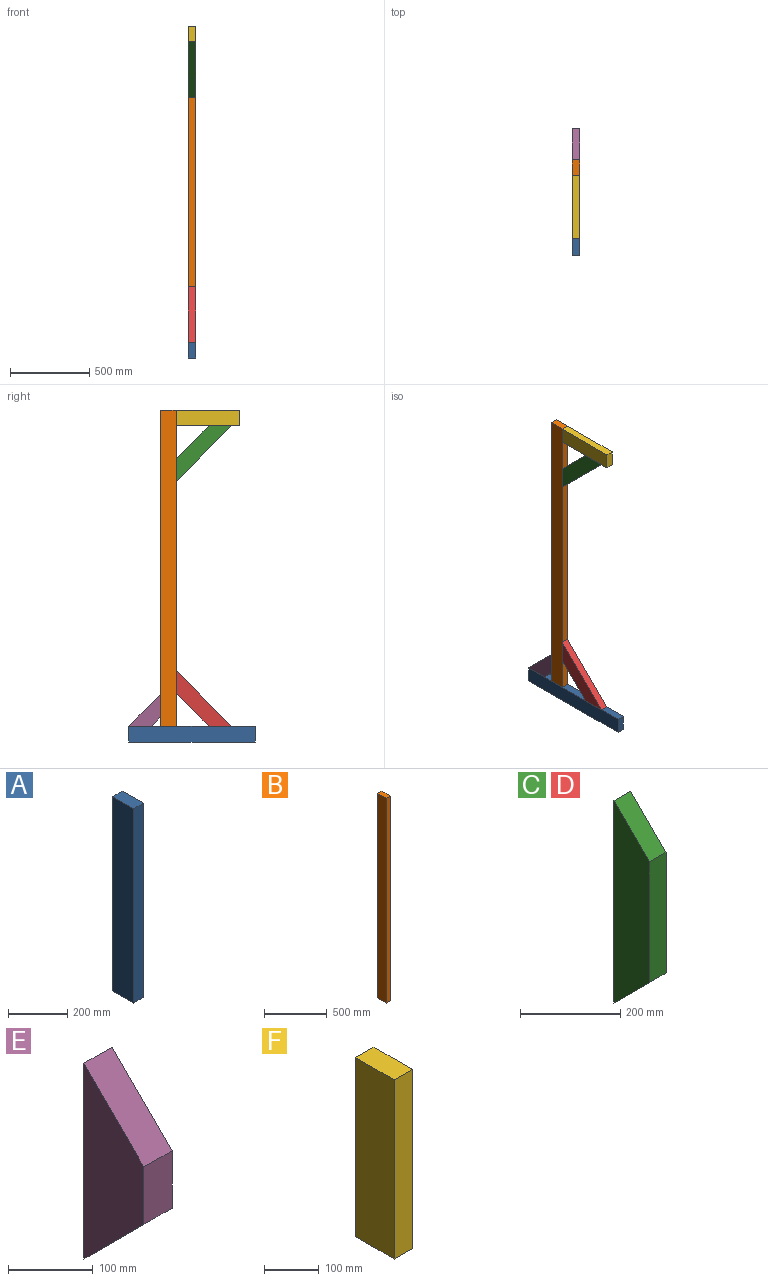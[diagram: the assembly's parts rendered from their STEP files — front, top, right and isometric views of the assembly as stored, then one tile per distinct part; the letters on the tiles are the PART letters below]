
ASSEMBLY  parts=6 mates=5
PART A: 6 faces, bbox 47x100x800 mm
  f0: plane 800x100mm, normal (-1,0,0), area 80000mm2, adj f1,f3,f4,f5
  f1: plane 800x47mm, normal (0,-1,0), area 37600mm2, adj f0,f2,f4,f5
  f2: plane 800x100mm, normal (1,0,0), area 80000mm2, adj f1,f3,f4,f5
  f3: plane 800x47mm, normal (0,1,0), area 37600mm2, adj f0,f2,f4,f5
  f4: plane 100x47mm, normal (0,0,1), area 4700mm2, adj f0,f1,f2,f3
  f5: plane 100x47mm, normal (0,0,-1), area 4700mm2, adj f0,f1,f2,f3
PART B: 6 faces, bbox 47x100x2000 mm
  f0: plane 2000x100mm, normal (-1,0,0), area 200000mm2, adj f1,f3,f4,f5
  f1: plane 2000x47mm, normal (0,-1,0), area 94000mm2, adj f0,f2,f4,f5
  f2: plane 2000x100mm, normal (1,0,0), area 200000mm2, adj f1,f3,f4,f5
  f3: plane 2000x47mm, normal (0,1,0), area 94000mm2, adj f0,f2,f4,f5
  f4: plane 100x47mm, normal (0,0,1), area 4700mm2, adj f0,f1,f2,f3
  f5: plane 100x47mm, normal (0,0,-1), area 4700mm2, adj f0,f1,f2,f3
PART C: 6 faces, bbox 47x100x495 mm
  f0: plane 494.97x100mm, normal (-1,0,0), area 39497.5mm2, adj f1,f3,f4,f5
  f1: plane 294.97x47mm, normal (0,-1,0), area 13863.8mm2, adj f0,f2,f4,f5
  f2: plane 494.97x100mm, normal (1,0,0), area 39497.5mm2, adj f1,f3,f4,f5
  f3: plane 494.97x47mm, normal (0,1,0), area 23263.8mm2, adj f0,f2,f4,f5
  f4: plane 100x100mm, normal (0,-0.71,-0.71), area 6646.8mm2, adj f0,f1,f2,f3
  f5: plane 100x100mm, normal (0,-0.71,0.71), area 6646.8mm2, adj f0,f1,f2,f3
PART D: same geometry as C
PART E: 6 faces, bbox 47x100x282.8 mm
  f0: plane 282.84x100mm, normal (-1,0,0), area 18284.3mm2, adj f1,f3,f4,f5
  f1: plane 82.84x47mm, normal (0,-1,0), area 3893.6mm2, adj f0,f2,f4,f5
  f2: plane 282.84x100mm, normal (1,0,0), area 18284.3mm2, adj f1,f3,f4,f5
  f3: plane 282.84x47mm, normal (0,1,0), area 13293.6mm2, adj f0,f2,f4,f5
  f4: plane 100x100mm, normal (0,-0.71,-0.71), area 6646.8mm2, adj f0,f1,f2,f3
  f5: plane 100x100mm, normal (0,-0.71,0.71), area 6646.8mm2, adj f0,f1,f2,f3
PART F: 6 faces, bbox 47x100x400 mm
  f0: plane 400x100mm, normal (-1,0,0), area 40000mm2, adj f1,f3,f4,f5
  f1: plane 400x47mm, normal (0,-1,0), area 18800mm2, adj f0,f2,f4,f5
  f2: plane 400x100mm, normal (1,0,0), area 40000mm2, adj f1,f3,f4,f5
  f3: plane 400x47mm, normal (0,1,0), area 18800mm2, adj f0,f2,f4,f5
  f4: plane 100x47mm, normal (0,0,1), area 4700mm2, adj f0,f1,f2,f3
  f5: plane 100x47mm, normal (0,0,-1), area 4700mm2, adj f0,f1,f2,f3
PLACE A rot(axis=(1,0,0),90deg) t=(-432.74,647.52,376.61)mm
PLACE B t=(-620.74,347.52,476.61)mm
PLACE C rot(axis=(-1,0,0),135deg) t=(-902.74,68.23,2447.32)mm
PLACE D rot(axis=(0,-0.38,-0.92),180deg) t=(84.26,68.23,405.9)mm
PLACE E rot(axis=(1,0,0),45deg) t=(-808.74,576.81,405.9)mm
PLACE F rot(axis=(-1,0,0),90deg) t=(-714.74,-52.48,2476.61)mm
MATE fastened F.f4 <-> B.f1  axis (0,1,0) through (-432.74,347.52,2476.61)mm
MATE fastened E.f5 <-> B.f3  axis (0,-1,0) through (-409.24,447.52,676.61)mm
MATE fastened C.f5 <-> B.f1  axis (0,1,0) through (-409.24,347.52,2026.61)mm
MATE fastened D.f5 <-> B.f1  axis (0,1,0) through (-409.24,347.52,826.61)mm
MATE fastened A.f2 <-> B.f2  axis (1,0,0) through (-385.74,397.52,476.61)mm
